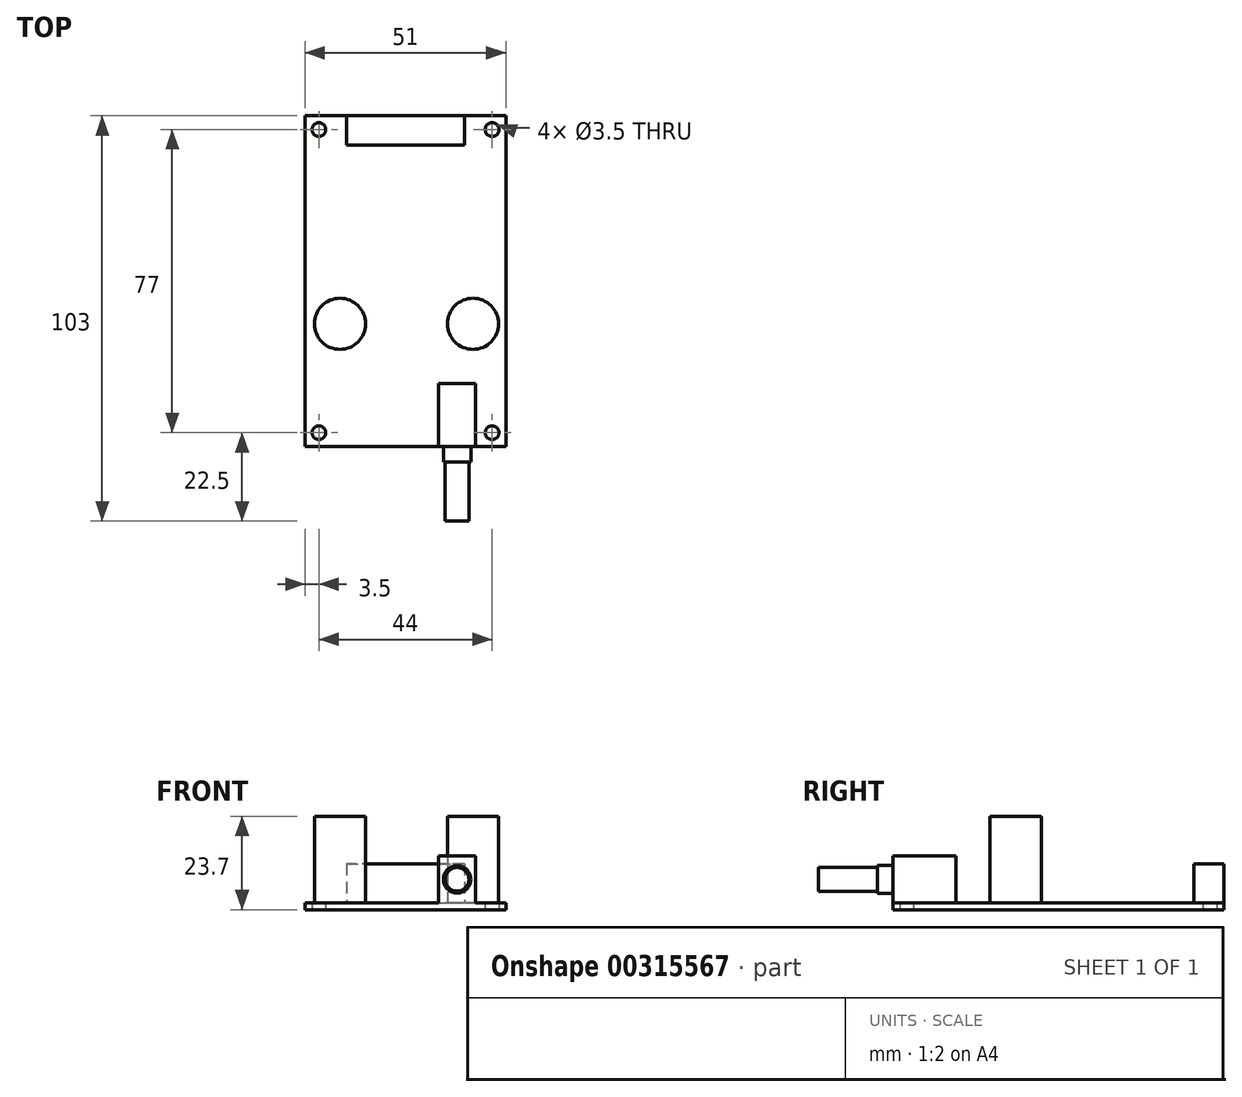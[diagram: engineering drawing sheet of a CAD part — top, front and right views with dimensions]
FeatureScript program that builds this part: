
annotation { "Feature Type Name" : "Feature", "Feature Type Description" : "" }
export const myFeature = defineFeature(function(context is Context, id is Id, definition is map)
    precondition{}
    {
        {
            var Q0;
            Q0=qCreatedBy(makeId("Top.planeOp"),FACE);
            var sketch = newSketch(context, id + "F0", { "sketchPlane" : qUnion([Q0])});
            skLineSegment(sketch, "E0.bottom", {"start": v(25.5, 42) * mm, "end": v(-25.5, 42) * mm});
            skLineSegment(sketch, "E0.top", {"start": v(25.5, -42) * mm, "end": v(-25.5, -42) * mm});
            skLineSegment(sketch, "E0.left", {"start": v(25.5, 42) * mm, "end": v(25.5, -42) * mm});
            skLineSegment(sketch, "E0.right", {"start": v(-25.5, 42) * mm, "end": v(-25.5, -42) * mm});
            skPoint(sketch, "E0.middle", {"position": v(0, 0) * mm});
            skCircle(sketch, "E1", {"center": v(-22, -38.5) * mm, "radius": 1.75 * mm});
            skLineSegment(sketch, "E2", {"start": v(0, 42) * mm, "end": v(0, -42) * mm, "construction": true});
            skLineSegment(sketch, "E3", {"start": v(-25.5, 0) * mm, "end": v(25.5, 0) * mm, "construction": true});
            skCircle(sketch, "E4.MirrorC", {"center": v(22, -38.5) * mm, "radius": 1.75 * mm});
            skCircle(sketch, "E5.MirrorC", {"center": v(22, 38.5) * mm, "radius": 1.75 * mm});
            skCircle(sketch, "E6.MirrorC", {"center": v(-22, 38.5) * mm, "radius": 1.75 * mm});
            skSolve(sketch);
        }
        {
            var Q0;
            Q0 = qSketchRegion(id + "F0", true);
            extrude(context, id + "F1", {"entities" : qUnion([Q0]), "depth" : 1.7 * mm});
        }
        {
            var Q0;
            Q0=makeQuery(id+"F1.opExtrude","CAP_FACE",FACE,{"disambiguationData":[OSD([sQuery(id+"F0.wireOp",EDGE,"E0.bottom"),sQuery(id+"F0.wireOp",EDGE,"E0.top"),sQuery(id+"F0.wireOp",EDGE,"E0.left"),sQuery(id+"F0.wireOp",EDGE,"E0.right"),sQuery(id+"F0.wireOp",EDGE,"E1"),sQuery(id+"F0.wireOp",EDGE,"E4.MirrorC"),sQuery(id+"F0.wireOp",EDGE,"E5.MirrorC"),sQuery(id+"F0.wireOp",EDGE,"E6.MirrorC")])],"isStart":false});
            var sketch = newSketch(context, id + "F2", { "sketchPlane" : qUnion([Q0])});
            skLineSegment(sketch, "E7.bottom", {"start": v(17.8, -42) * mm, "end": v(8.4, -42) * mm});
            skLineSegment(sketch, "E7.top", {"start": v(17.8, -26) * mm, "end": v(8.4, -26) * mm});
            skLineSegment(sketch, "E7.left", {"start": v(17.8, -42) * mm, "end": v(17.8, -26) * mm});
            skLineSegment(sketch, "E7.right", {"start": v(8.4, -42) * mm, "end": v(8.4, -26) * mm});
            skSolve(sketch);
        }
        {
            var Q0;
            Q0 = qSketchRegion(id + "F2", true);
            extrude(context, id + "F3", {"entities" : qUnion([Q0]), "operationType" : NewBodyOperationType.ADD, "depth" : 12 * mm});
        }
        {
            var Q0;
            Q0=makeQuery(id+"F3.opExtrude","SWEPT_FACE",FACE,{"disambiguationData":[OSD([sQuery(id+"F2.wireOp",EDGE,"E7.bottom")])]});
            var sketch = newSketch(context, id + "F4", { "sketchPlane" : qUnion([Q0])});
            skLineSegment(sketch, "E8", {"start": v(8.4, 13.7) * mm, "end": v(17.8, 1.7) * mm, "construction": true});
            skCircle(sketch, "E9", {"center": v(13.1, 7.7) * mm, "radius": 3.5 * mm});
            skSolve(sketch);
        }
        {
            var Q0;
            Q0 = qSketchRegion(id + "F4", true);
            extrude(context, id + "F5", {"entities" : qUnion([Q0]), "operationType" : NewBodyOperationType.ADD, "depth" : 19 * mm, "hasDraft" : true, "draftAngle" : 0 * degree, "draftPullDirection" : true});
        }
        {
            var Q0;
            Q0=makeQuery(id+"F1.opExtrude","CAP_FACE",FACE,{"disambiguationData":[OSD([sQuery(id+"F0.wireOp",EDGE,"E0.bottom"),sQuery(id+"F0.wireOp",EDGE,"E0.top"),sQuery(id+"F0.wireOp",EDGE,"E0.left"),sQuery(id+"F0.wireOp",EDGE,"E0.right"),sQuery(id+"F0.wireOp",EDGE,"E1"),sQuery(id+"F0.wireOp",EDGE,"E4.MirrorC"),sQuery(id+"F0.wireOp",EDGE,"E5.MirrorC"),sQuery(id+"F0.wireOp",EDGE,"E6.MirrorC")])],"isStart":false});
            var sketch = newSketch(context, id + "F6", { "sketchPlane" : qUnion([Q0])});
            skCircle(sketch, "E10", {"center": v(17.15, -10.85) * mm, "radius": 6.5 * mm});
            skCircle(sketch, "E11", {"center": v(-16.64, -10.85) * mm, "radius": 6.5 * mm});
            skSolve(sketch);
        }
        {
            var Q0;
            Q0 = qSketchRegion(id + "F6", true);
            extrude(context, id + "F7", {"entities" : qUnion([Q0]), "operationType" : NewBodyOperationType.ADD, "depth" : 22 * mm});
        }
        {
            var Q0;
            Q0=makeQuery(id+"F1.opExtrude","CAP_FACE",FACE,{"disambiguationData":[OSD([sQuery(id+"F0.wireOp",EDGE,"E0.bottom"),sQuery(id+"F0.wireOp",EDGE,"E0.top"),sQuery(id+"F0.wireOp",EDGE,"E0.left"),sQuery(id+"F0.wireOp",EDGE,"E0.right"),sQuery(id+"F0.wireOp",EDGE,"E1"),sQuery(id+"F0.wireOp",EDGE,"E4.MirrorC"),sQuery(id+"F0.wireOp",EDGE,"E5.MirrorC"),sQuery(id+"F0.wireOp",EDGE,"E6.MirrorC")])],"isStart":false});
            var sketch = newSketch(context, id + "F8", { "sketchPlane" : qUnion([Q0])});
            skLineSegment(sketch, "E12.bottom", {"start": v(-15, 42) * mm, "end": v(15, 42) * mm});
            skLineSegment(sketch, "E12.top", {"start": v(-15, 34.5) * mm, "end": v(15, 34.5) * mm});
            skLineSegment(sketch, "E12.left", {"start": v(-15, 42) * mm, "end": v(-15, 34.5) * mm});
            skLineSegment(sketch, "E12.right", {"start": v(15, 42) * mm, "end": v(15, 34.5) * mm});
            skLineSegment(sketch, "E13", {"start": v(0, 42) * mm, "end": v(0, -23.13) * mm, "construction": true});
            skSolve(sketch);
        }
        {
            var Q0;
            Q0 = qSketchRegion(id + "F8", true);
            extrude(context, id + "F9", {"entities" : qUnion([Q0]), "operationType" : NewBodyOperationType.ADD, "depth" : 10 * mm});
        }
        {
            var Q0;
            Q0=makeQuery(id+"F5.opExtrude","CAP_FACE",FACE,{"disambiguationData":[OSD([sQuery(id+"F4.wireOp",EDGE,"E9")])],"isStart":false});
            var sketch = newSketch(context, id + "F10", { "sketchPlane" : qUnion([Q0])});
            skCircle(sketch, "E14", {"center": v(13.1, 7.7) * mm, "radius": 3 * mm});
            skCircle(sketch, "E15", {"center": v(13.1, 7.7) * mm, "radius": 5.94 * mm});
            skSolve(sketch);
        }
        {
            var Q0;
            Q0 = qSketchRegion(id + "F10", true);
            extrude(context, id + "F11", {"entities" : qUnion([Q0]), "operationType" : NewBodyOperationType.REMOVE, "oppositeDirection" : true, "depth" : 15 * mm});
        }
    });
